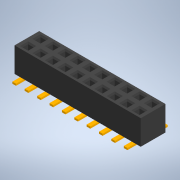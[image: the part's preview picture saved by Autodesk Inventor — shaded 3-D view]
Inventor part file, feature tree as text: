
AUTODESK INVENTOR PART (.ipt)
format: ipt  version: 2022 (Build 260153000, 153)  size: 596,480 bytes
history: native  units: mm
features: extrude x2, sketch x2, other x1, chamfer x1, projected_geometry x1
ambient origin geometry x8: Origin, YZ Plane, XZ Plane, XY Plane, X Axis, Y Axis, Z Axis, Center Point
bodies: Body1 (feature_tree)
feature tree (7):
  other  "Твердое тело1"
  extrude  "Выдавливание1"  Depth=20.4mm
  chamfer  "Фаска1"  Distance=4.0mm
  extrude  "Выдавливание2"  Depth=18.0mm
  sketch  "Эскиз1"
  sketch  "Эскиз2"
  projected_geometry  "Спроецированная петля1"
